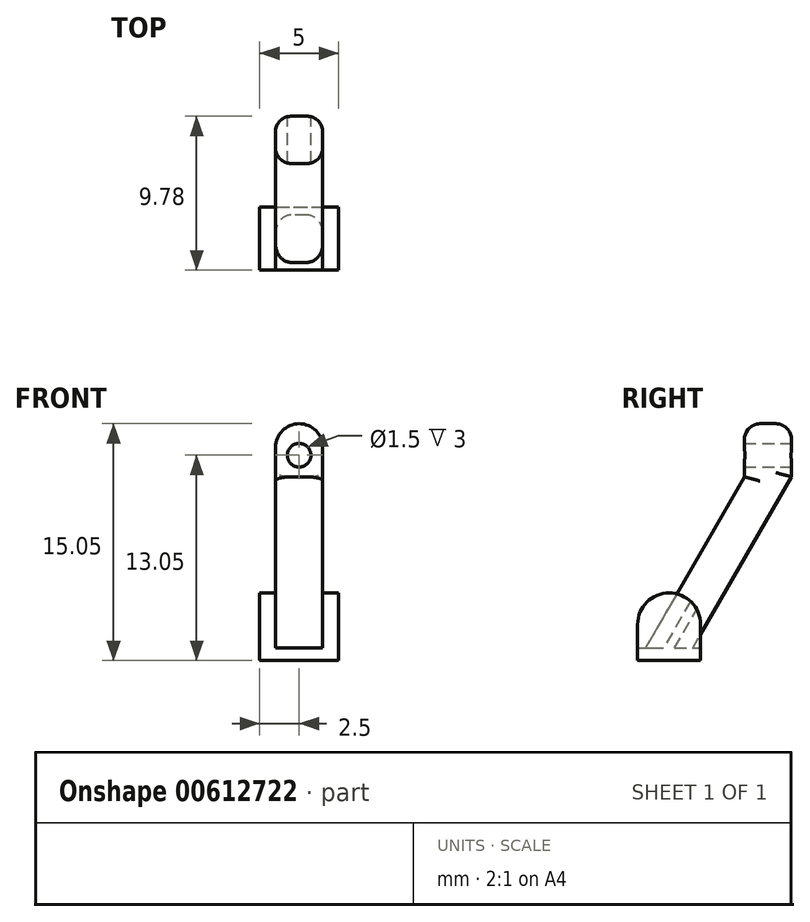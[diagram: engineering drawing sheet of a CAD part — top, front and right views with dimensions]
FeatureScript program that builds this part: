
annotation { "Feature Type Name" : "Feature", "Feature Type Description" : "" }
export const myFeature = defineFeature(function(context is Context, id is Id, definition is map)
    precondition{}
    {
        {
            var Q0;
            Q0=qCreatedBy(makeId("Top.planeOp"),FACE);
            var sketch = newSketch(context, id + "F0", { "sketchPlane" : qUnion([Q0])});
            skLineSegment(sketch, "E0.bottom", {"start": v(0, 0) * mm, "end": v(5, 0) * mm});
            skLineSegment(sketch, "E0.top", {"start": v(0, 4) * mm, "end": v(5, 4) * mm});
            skLineSegment(sketch, "E0.left", {"start": v(0, 0) * mm, "end": v(0, 4) * mm});
            skLineSegment(sketch, "E0.right", {"start": v(5, 0) * mm, "end": v(5, 4) * mm});
            skSolve(sketch);
        }
        {
            var Q0;
            Q0=qSketchRegion(id+"F0",true);
            extrude(context, id + "F1", {"entities" : qUnion([Q0]), "depth" : 0.8 * mm, "offsetDistance" : 25 * mm});
        }
        {
            var Q0;
            Q0=qCreatedBy(makeId("Right.planeOp"),FACE);
            cPlane(context, id + "F2", {"entities" : qUnion([Q0]), "cplaneType" : CPlaneType.OFFSET, "offset" : 2.5 * mm, "width" : 150 * mm, "height" : 150 * mm});
        }
        {
            var Q0;
            Q0=qCreatedBy(id+"F2.planeOp",FACE);
            var sketch = newSketch(context, id + "F3", { "sketchPlane" : qUnion([Q0])});
            skLineSegment(sketch, "E1", {"start": v(3.5, 0.8) * mm, "end": v(9.78, 11.68) * mm});
            skLineSegment(sketch, "E2", {"start": v(6.78, 11.68) * mm, "end": v(0.5, 0.8) * mm});
            skLineSegment(sketch, "E3", {"start": v(0.5, 0.8) * mm, "end": v(3.5, 0.8) * mm});
            skLineSegment(sketch, "E4", {"start": v(6.78, 11.68) * mm, "end": v(6.78, 15.05) * mm});
            skLineSegment(sketch, "E5", {"start": v(6.78, 15.05) * mm, "end": v(9.78, 15.05) * mm});
            skLineSegment(sketch, "E6", {"start": v(9.78, 15.05) * mm, "end": v(9.78, 11.68) * mm});
            skLineSegment(sketch, "E7", {"start": v(6.78, 11.68) * mm, "end": v(14.52, 11.68) * mm, "construction": true});
            skSolve(sketch);
        }
        {
            var Q0;
            Q0=qSketchRegion(id+"F3",true);
            extrude(context, id + "F4", {"entities" : qUnion([Q0]), "operationType" : NewBodyOperationType.ADD, "endBound" : BoundingType.SYMMETRIC, "depth" : 3 * mm, "offsetDistance" : 25 * mm});
        }
        {
            var Q0;
            Q0=makeQuery(id+"F4.opExtrude","SWEPT_FACE",FACE,{"disambiguationData":[OSD([sQuery(id+"F3.wireOp",EDGE,"E6")])]});
            var sketch = newSketch(context, id + "F5", { "sketchPlane" : qUnion([Q0])});
            skCircle(sketch, "E8", {"center": v(-2.5, 13.05) * mm, "radius": 0.75 * mm});
            skSolve(sketch);
        }
        {
            var Q0;
            Q0=qSketchRegion(id+"F5",true);
            extrude(context, id + "F6", {"entities" : qUnion([Q0]), "operationType" : NewBodyOperationType.REMOVE, "endBound" : BoundingType.THROUGH_ALL, "oppositeDirection" : true, "depth" : 25 * mm, "offsetDistance" : 25 * mm});
        }
        {
            var Q0;
            Q0=makeQuery(id+"F4.opExtrude","CAP_EDGE",EDGE,{"disambiguationData":[OSD([sQuery(id+"F3.wireOp",EDGE,"E5")])],"isStart":true});
            var Q1;
            Q1=makeQuery(id+"F4.opExtrude","CAP_EDGE",EDGE,{"disambiguationData":[OSD([sQuery(id+"F3.wireOp",EDGE,"E5")])],"isStart":false});
            fillet(context, id + "F7", {"entities" : qUnion([Q0, Q1]), "radius" : 1.5 * mm, "tangentPropagation" : true, "allowEdgeOverflow" : false});
        }
        {
            var Q0;
            Q0=makeQuery(id+"F4.opExtrude","CAP_EDGE",EDGE,{"disambiguationData":[OSD([sQuery(id+"F3.wireOp",EDGE,"E1")])],"isStart":true});
            var Q1;
            Q1=makeQuery(id+"F4.opExtrude","CAP_EDGE",EDGE,{"disambiguationData":[OSD([sQuery(id+"F3.wireOp",EDGE,"E6")])],"isStart":true});
            var Q2;
            Q2=makeQuery(id+"F7.opFillet","BLEND_EDGE",EDGE,{"blendedFrom":[makeQuery(id+"F4.opExtrude","CAP_EDGE",EDGE,{"disambiguationData":[OSD([sQuery(id+"F3.wireOp",EDGE,"E5")])],"isStart":false}),makeQuery(id+"F4.opExtrude","SWEPT_FACE",FACE,{"disambiguationData":[OSD([sQuery(id+"F3.wireOp",EDGE,"E6")])]})],"blendedInto":[makeQuery(id+"F4.opExtrude","SWEPT_FACE",FACE,{"disambiguationData":[OSD([sQuery(id+"F3.wireOp",EDGE,"E6")])]})]});
            var Q3;
            Q3=makeQuery(id+"F4.opExtrude","CAP_EDGE",EDGE,{"disambiguationData":[OSD([sQuery(id+"F3.wireOp",EDGE,"E1")])],"isStart":false});
            var Q4;
            Q4=makeQuery(id+"F4.opExtrude","CAP_EDGE",EDGE,{"disambiguationData":[OSD([sQuery(id+"F3.wireOp",EDGE,"E2")])],"isStart":true});
            var Q5;
            Q5=makeQuery(id+"F4.opExtrude","CAP_EDGE",EDGE,{"disambiguationData":[OSD([sQuery(id+"F3.wireOp",EDGE,"E4")])],"isStart":true});
            var Q6;
            Q6=makeQuery(id+"F4.opExtrude","CAP_EDGE",EDGE,{"disambiguationData":[OSD([sQuery(id+"F3.wireOp",EDGE,"E2")])],"isStart":false});
            fillet(context, id + "F8", {"entities" : qUnion([Q0, Q1, Q2, Q3, Q4, Q5, Q6]), "radius" : 1 * mm, "tangentPropagation" : true, "allowEdgeOverflow" : false});
        }
        {
            var Q0;
            Q0=makeQuery(id+"F1.opExtrude","SWEPT_FACE",FACE,{"disambiguationData":[OSD([sQuery(id+"F0.wireOp",EDGE,"E0.left")])]});
            var sketch = newSketch(context, id + "F9", { "sketchPlane" : qUnion([Q0])});
            skLineSegment(sketch, "E9.bottom", {"start": v(-4, 0.8) * mm, "end": v(0, 0.8) * mm});
            skLineSegment(sketch, "E9.top", {"start": v(-2, 4.3) * mm, "end": v(-2, 4.3) * mm});
            skLineSegment(sketch, "E9.left", {"start": v(-4, 0.8) * mm, "end": v(-4, 2.3) * mm});
            skLineSegment(sketch, "E9.right", {"start": v(0, 0.8) * mm, "end": v(0, 2.3) * mm});
            skPoint(sketch, "E10.visualSharp", {"position": v(-4, 4.3) * mm});
            skArc(sketch, "E10.filletArc", {"start": v(-2, 4.3) * mm, "mid": v(-3.41, 3.71) * mm, "end": v(-4, 2.3) * mm});
            skPoint(sketch, "E11.visualSharp", {"position": v(0, 4.3) * mm});
            skArc(sketch, "E11.filletArc", {"start": v(0, 2.3) * mm, "mid": v(-0.59, 3.71) * mm, "end": v(-2, 4.3) * mm});
            skSolve(sketch);
        }
        {
            var Q0;
            Q0=qSketchRegion(id+"F9",true);
            extrude(context, id + "F10", {"entities" : qUnion([Q0]), "oppositeDirection" : true, "depth" : 1 * mm, "offsetDistance" : 25 * mm});
        }
        {
            var Q0;
            Q0=makeQuery(id+"F10.opExtrude","SWEPT_BODY",BODY,{"disambiguationData":[OSD([sQuery(id+"F9.wireOp",EDGE,"E9.bottom"),sQuery(id+"F9.wireOp",EDGE,"E9.left"),sQuery(id+"F9.wireOp",EDGE,"E9.right"),sQuery(id+"F9.wireOp",EDGE,"E10.filletArc"),sQuery(id+"F9.wireOp",EDGE,"E11.filletArc")])]});
            var Q1;
            Q1=qCreatedBy(id+"F2.planeOp",FACE);
            mirror(context, id + "F11", {"operationType" : NewBodyOperationType.ADD, "entities" : qUnion([Q0]), "mirrorPlane" : qUnion([Q1])});
        }
    });
